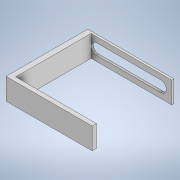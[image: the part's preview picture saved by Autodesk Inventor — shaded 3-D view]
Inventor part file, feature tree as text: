
AUTODESK INVENTOR PART (.ipt)
format: ipt  version: 2021 (Build 250183000, 183)  size: 125,440 bytes
history: native  units: mm
features: extrude x4, sketch x4, other x1
ambient origin geometry x8: Origin, YZ Plane, XZ Plane, XY Plane, X Axis, Y Axis, Z Axis, Center Point
bodies: Body1 (feature_tree)
feature tree (9):
  other  "Sólido1"
  extrude  "Extrusão1"  Depth=10.0mm
  extrude  "Extrusão2"  Depth=1.0mm
  extrude  "Extrusão3"  Depth=1.0mm TaperAngle=0.0deg
  extrude  "Extrusão4"  Depth=35.0mm TaperAngle=0.0deg
  sketch  "Esboço1"  dims[d0=40.0mm d1=10.0mm]
  sketch  "Esboço2"  dims[d2=1.0mm d3=0.0mm d4=30.0mm]
  sketch  "Esboço3"  dims[d5=5.0mm d6=1.0mm d7=0.0mm]
  sketch  "Esboço4"  dims[d8=2.5mm d9=35.0mm d10=0.0mm d11=2.0mm d12=0.0mm]
